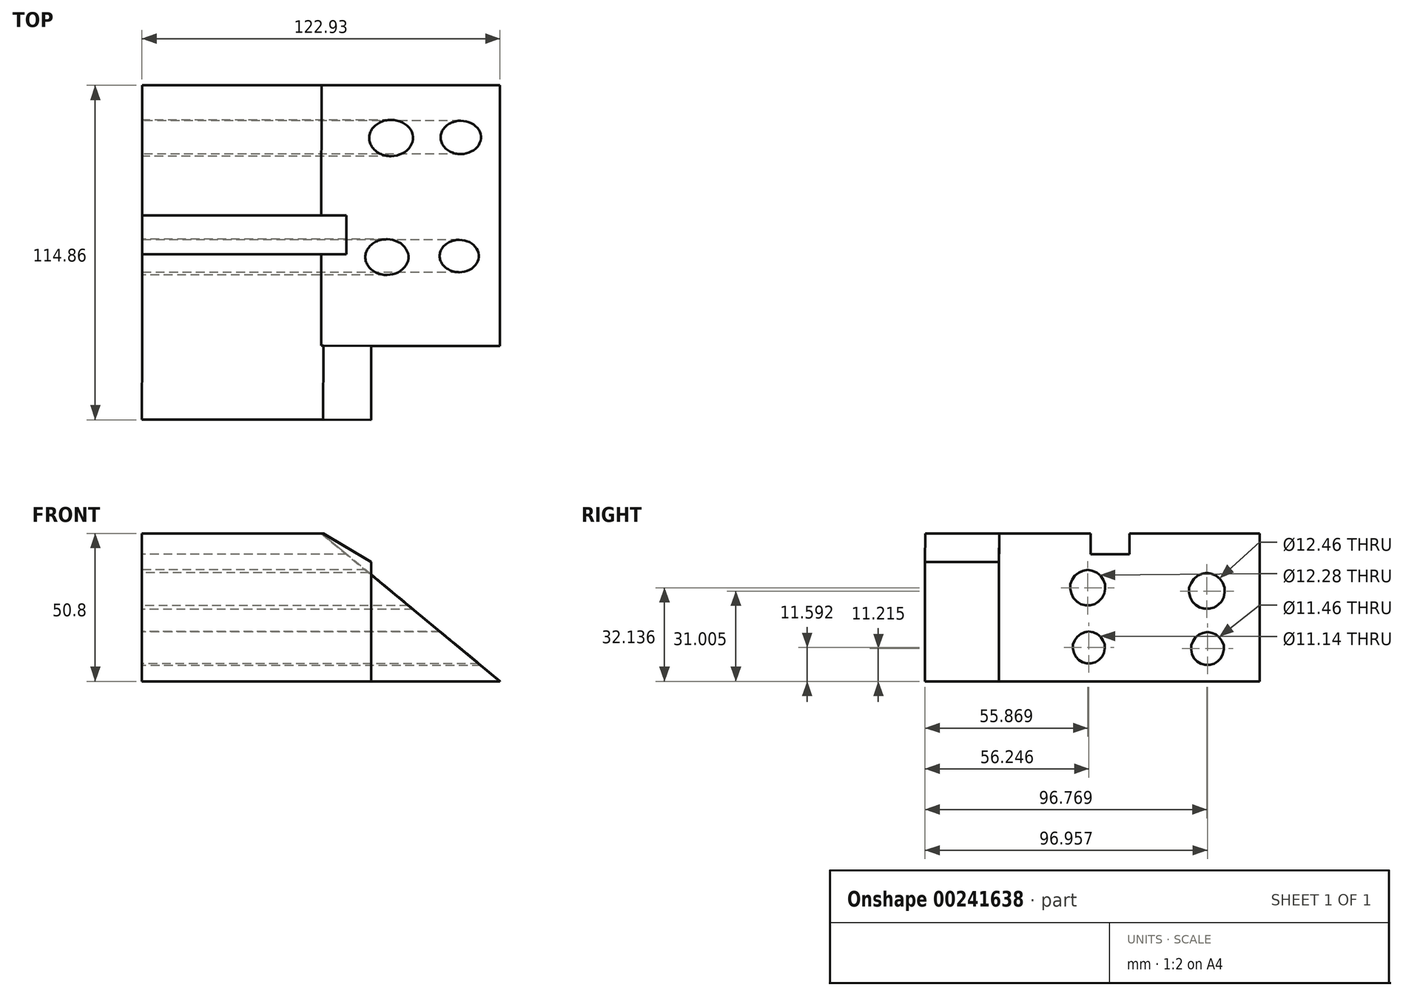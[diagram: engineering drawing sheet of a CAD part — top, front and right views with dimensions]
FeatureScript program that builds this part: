
annotation { "Feature Type Name" : "Feature", "Feature Type Description" : "" }
export const myFeature = defineFeature(function(context is Context, id is Id, definition is map)
    precondition{}
    {
        {
            var Q0;
            Q0=qCreatedBy(makeId("Top.planeOp"),FACE);
            var sketch = newSketch(context, id + "F0", { "sketchPlane" : qUnion([Q0])});
            skLineSegment(sketch, "E0", {"start": v(-62.3, -36.38) * mm, "end": v(-62.3, 52.96) * mm});
            skLineSegment(sketch, "E1", {"start": v(-62.3, 52.96) * mm, "end": v(60.6, 52.96) * mm});
            skLineSegment(sketch, "E2", {"start": v(60.6, 52.96) * mm, "end": v(60.6, -36.57) * mm});
            skLineSegment(sketch, "E3", {"start": v(-62.3, -36.38) * mm, "end": v(60.6, -36.57) * mm});
            skSolve(sketch);
        }
        {
            var Q0;
            Q0 = qSketchRegion(id + "F0", true);
            extrude(context, id + "F1", {"entities" : qUnion([Q0]), "depth" : 50.8 * mm});
        }
        {
            var Q0;
            Q0=makeQuery(id+"F1.opExtrude","SWEPT_FACE",FACE,{"disambiguationData":[OSD([sQuery(id+"F0.wireOp",EDGE,"E3")])]});
            var sketch = newSketch(context, id + "F2", { "sketchPlane" : qUnion([Q0])});
            skLineSegment(sketch, "E4", {"start": v(-0.8, 50.8) * mm, "end": v(60.65, 0) * mm});
            skSolve(sketch);
        }
        {
            var Q0;
            {var subQ0=sQuery(id+"F2.wireOp",EDGE,"E4");Q0=makeQuery(id+"F2.imprint","IMPRINT",FACE,{"disambiguationData":[TD([[makeQuery(id+"F2.imprint","IMPRINT",EDGE,{"derivedFrom":subQ0}),1.0]])]});}
            extrude(context, id + "F3", {"entities" : qUnion([Q0]), "operationType" : NewBodyOperationType.ADD, "endBound" : BoundingType.THROUGH_ALL, "depth" : 25.4 * mm});
        }
        {
            var Q0;
            Q0=makeQuery(id+"F3.opExtrude","CAP_FACE",FACE,{"disambiguationData":[OSD([sQuery(id+"F0.wireOp",EDGE,"E2"),sQuery(id+"F0.wireOp",EDGE,"E3"),sQuery(id+"F2.wireOp",EDGE,"E4")])],"isStart":false});
            extrude(context, id + "F4", {"entities" : qUnion([Q0]), "operationType" : NewBodyOperationType.REMOVE, "endBound" : BoundingType.THROUGH_ALL, "oppositeDirection" : true, "depth" : 25.4 * mm});
        }
        {
            var Q0;
            Q0=makeQuery(id+"F1.opExtrude","SWEPT_FACE",FACE,{"disambiguationData":[OSD([sQuery(id+"F0.wireOp",EDGE,"E0")])]});
            var sketch = newSketch(context, id + "F5", { "sketchPlane" : qUnion([Q0])});
            skLineSegment(sketch, "E5", {"start": v(-8.3, 50.8) * mm, "end": v(-8.3, 43.63) * mm});
            skPoint(sketch, "E5.endSnap0", {"position": v(-8.3, 50.8) * mm});
            skLineSegment(sketch, "E6", {"start": v(-8.3, 43.63) * mm, "end": v(5.09, 43.63) * mm});
            skLineSegment(sketch, "E7", {"start": v(5.09, 43.63) * mm, "end": v(5.09, 50.8) * mm});
            skSolve(sketch);
        }
        {
            var Q0;
            {var subQ0=sQuery(id+"F5.wireOp",EDGE,"E5");Q0=makeQuery(id+"F5.imprint","IMPRINT",FACE,{"disambiguationData":[TD([[makeQuery(id+"F5.imprint","IMPRINT",EDGE,{"derivedFrom":subQ0}),1.0]])]});}
            extrude(context, id + "F6", {"entities" : qUnion([Q0]), "operationType" : NewBodyOperationType.REMOVE, "endBound" : BoundingType.THROUGH_ALL, "oppositeDirection" : true, "depth" : 25.4 * mm});
        }
        {
            var Q0;
            Q0=makeQuery(id+"F1.opExtrude","SWEPT_FACE",FACE,{"disambiguationData":[OSD([sQuery(id+"F0.wireOp",EDGE,"E3")])]});
            var sketch = newSketch(context, id + "F7", { "sketchPlane" : qUnion([Q0])});
            skLineSegment(sketch, "E8.bottom", {"start": v(-62.24, 50.8) * mm, "end": v(16.43, 50.8) * mm});
            skLineSegment(sketch, "E8.top", {"start": v(-62.24, 0) * mm, "end": v(16.43, 0) * mm});
            skLineSegment(sketch, "E8.left", {"start": v(-62.24, 50.8) * mm, "end": v(-62.24, 0) * mm});
            skLineSegment(sketch, "E8.right", {"start": v(16.43, 50.8) * mm, "end": v(16.43, 0) * mm});
            skSolve(sketch);
        }
        {
            var Q0;
            Q0 = qSketchRegion(id + "F7", true);
            extrude(context, id + "F8", {"entities" : qUnion([Q0]), "operationType" : NewBodyOperationType.ADD, "depth" : 25.4 * mm});
        }
        {
            var Q0;
            Q0=makeQuery(id+"F8.opExtrude","CAP_FACE",FACE,{"disambiguationData":[OSD([sQuery(id+"F7.wireOp",EDGE,"E8.bottom"),sQuery(id+"F7.wireOp",EDGE,"E8.top"),sQuery(id+"F7.wireOp",EDGE,"E8.left"),sQuery(id+"F7.wireOp",EDGE,"E8.right")])],"isStart":false});
            var sketch = newSketch(context, id + "F9", { "sketchPlane" : qUnion([Q0])});
            skLineSegment(sketch, "E9", {"start": v(0, 50.8) * mm, "end": v(16.43, 40.94) * mm});
            skSolve(sketch);
        }
        {
            var Q0;
            {var subQ0=sQuery(id+"F9.wireOp",EDGE,"E9");Q0=makeQuery(id+"F9.imprint","IMPRINT",FACE,{"disambiguationData":[TD([[makeQuery(id+"F9.imprint","IMPRINT",EDGE,{"derivedFrom":subQ0}),1.0]])]});}
            extrude(context, id + "F10", {"entities" : qUnion([Q0]), "operationType" : NewBodyOperationType.REMOVE, "oppositeDirection" : true, "depth" : 25.4 * mm});
        }
        {
            var Q0;
            Q0=makeQuery(id+"F1.opExtrude","SWEPT_FACE",FACE,{"disambiguationData":[OSD([sQuery(id+"F0.wireOp",EDGE,"E0")])]});
            var sketch = newSketch(context, id + "F11", { "sketchPlane" : qUnion([Q0])});
            skCircle(sketch, "E10", {"center": v(-34.87, 31) * mm, "radius": 6.23 * mm});
            skCircle(sketch, "E11", {"center": v(-34.5, 15.55) * mm, "radius": 6.03 * mm});
            skCircle(sketch, "E12", {"center": v(5.47, 31.95) * mm, "radius": 6.36 * mm});
            skCircle(sketch, "E13", {"center": v(5.47, 14.98) * mm, "radius": 6.64 * mm});
            skSolve(sketch);
        }
        {
            var Q0;
            Q0=makeQuery(id+"F11.imprint","IMPRINT",FACE,{"disambiguationData":[TD([[makeQuery(id+"F11.imprint","IMPRINT",EDGE,{"derivedFrom":sQuery(id+"F11.wireOp",EDGE,"E10")}),1.0]])]});
            extrude(context, id + "F12", {"entities" : qUnion([Q0]), "operationType" : NewBodyOperationType.REMOVE, "endBound" : BoundingType.THROUGH_ALL, "oppositeDirection" : true, "depth" : 25.4 * mm});
        }
        {
            var Q0;
            Q0=makeQuery(id+"F1.opExtrude","SWEPT_FACE",FACE,{"disambiguationData":[OSD([sQuery(id+"F0.wireOp",EDGE,"E0")])]});
            var sketch = newSketch(context, id + "F13", { "sketchPlane" : qUnion([Q0])});
            skCircle(sketch, "E14", {"center": v(6.03, 32.14) * mm, "radius": 6.14 * mm});
            skSolve(sketch);
        }
        {
            var Q0;
            Q0 = qSketchRegion(id + "F13", true);
            extrude(context, id + "F14", {"entities" : qUnion([Q0]), "operationType" : NewBodyOperationType.REMOVE, "endBound" : BoundingType.THROUGH_ALL, "oppositeDirection" : true, "depth" : 25.4 * mm});
        }
        {
            var Q0;
            Q0=makeQuery(id+"F1.opExtrude","SWEPT_FACE",FACE,{"disambiguationData":[OSD([sQuery(id+"F0.wireOp",EDGE,"E0")])]});
            var sketch = newSketch(context, id + "F15", { "sketchPlane" : qUnion([Q0])});
            skCircle(sketch, "E15", {"center": v(-35.06, 11.21) * mm, "radius": 5.73 * mm});
            skSolve(sketch);
        }
        {
            var Q0;
            Q0=makeQuery(id+"F15.imprint","IMPRINT",FACE,{"disambiguationData":[TD([[makeQuery(id+"F15.imprint","IMPRINT",EDGE,{"derivedFrom":sQuery(id+"F15.wireOp",EDGE,"E15")}),1.0]])]});
            extrude(context, id + "F16", {"entities" : qUnion([Q0]), "operationType" : NewBodyOperationType.REMOVE, "endBound" : BoundingType.THROUGH_ALL, "oppositeDirection" : true, "depth" : 25.4 * mm});
        }
        {
            var Q0;
            Q0=makeQuery(id+"F1.opExtrude","SWEPT_FACE",FACE,{"disambiguationData":[OSD([sQuery(id+"F0.wireOp",EDGE,"E0")])]});
            var sketch = newSketch(context, id + "F17", { "sketchPlane" : qUnion([Q0])});
            skCircle(sketch, "E16", {"center": v(5.65, 11.6) * mm, "radius": 5.57 * mm});
            skSolve(sketch);
        }
        {
            var Q0;
            Q0=makeQuery(id+"F17.imprint","IMPRINT",FACE,{"disambiguationData":[TD([[makeQuery(id+"F17.imprint","IMPRINT",EDGE,{"derivedFrom":sQuery(id+"F17.wireOp",EDGE,"E16")}),1.0]])]});
            extrude(context, id + "F18", {"entities" : qUnion([Q0]), "operationType" : NewBodyOperationType.REMOVE, "endBound" : BoundingType.THROUGH_ALL, "oppositeDirection" : true, "depth" : 25.4 * mm});
        }
    });
